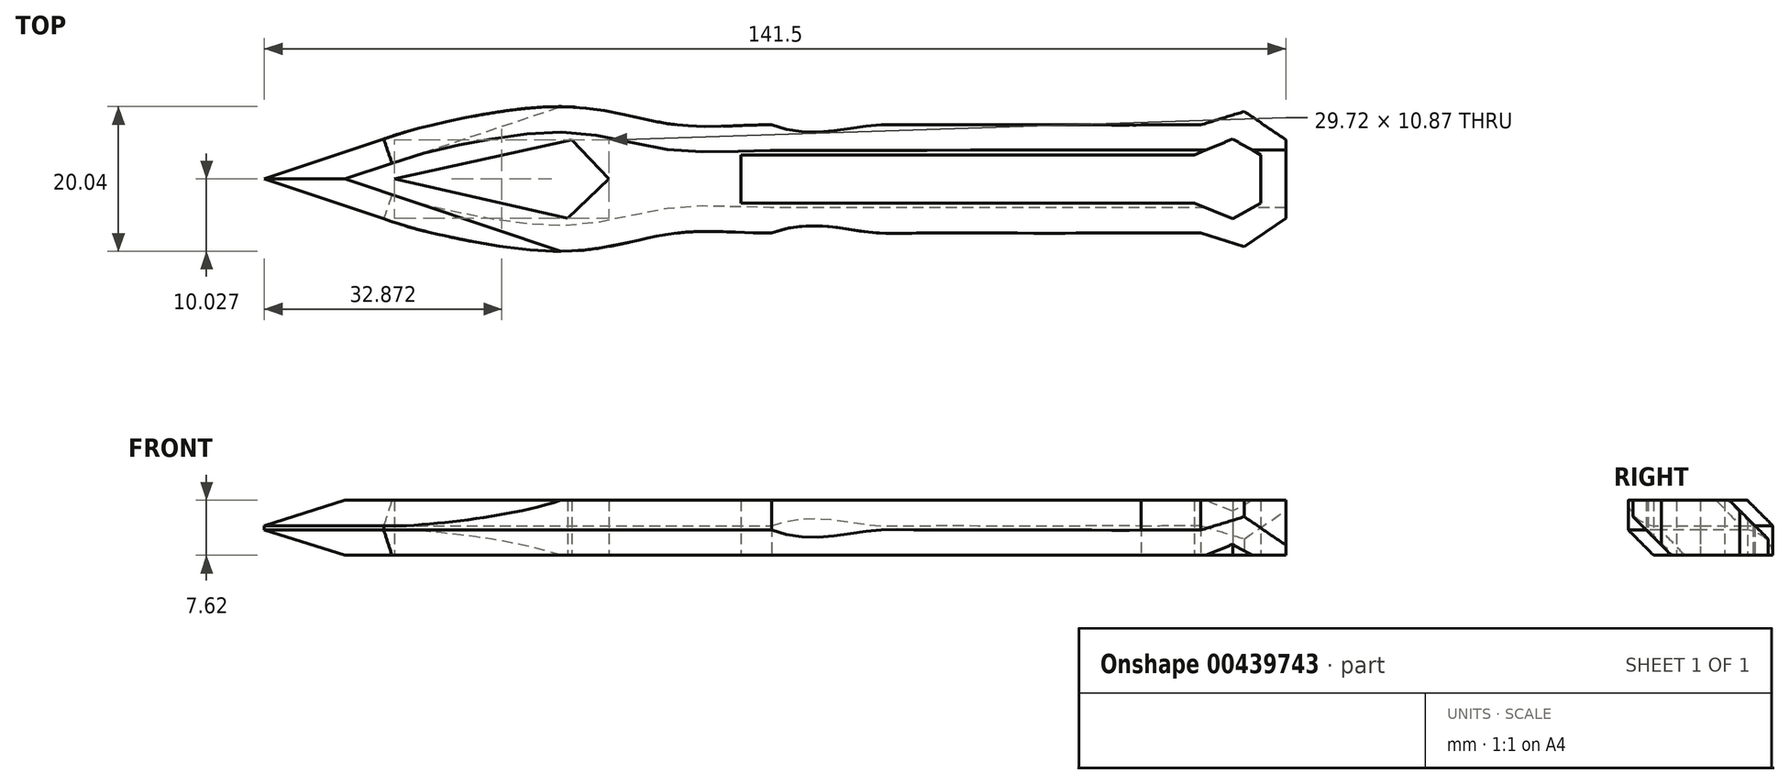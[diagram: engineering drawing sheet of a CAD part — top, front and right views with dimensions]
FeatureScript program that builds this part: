
annotation { "Feature Type Name" : "Feature", "Feature Type Description" : "" }
export const myFeature = defineFeature(function(context is Context, id is Id, definition is map)
    precondition{}
    {
        {
            var Q0;
            Q0=qCreatedBy(makeId("Top.planeOp"),FACE);
            var sketch = newSketch(context, id + "F0", { "sketchPlane" : qUnion([Q0])});
            skLineSegment(sketch, "E0", {"start": v(-70.25, 0) * mm, "end": v(-53.73, 5.53) * mm});
            skFitSpline(sketch, "E1", {"points": [v(-53.73, 5.53) * mm, v(-46.23, 7.66) * mm, v(-27.9, 9.99) * mm, v(-13.2, 7.5) * mm, v(0, 7.5) * mm], "startDerivative": vector(45.2, 15.8) * mm, "endDerivative": vector(54.18, 0.03) * mm});
            skFitSpline(sketch, "E2", {"points": [v(0, 7.5) * mm, v(12.65, 7.26) * mm, v(20.34, 7.5) * mm, v(42.69, 7.5) * mm, v(51.18, 7.5) * mm], "startDerivative": vector(56.8, -21.67) * mm, "endDerivative": vector(32.3, 1.6) * mm});
            skLineSegment(sketch, "E3.MirrorCS", {"start": v(-70.25, 0) * mm, "end": v(-53.73, -5.53) * mm});
            skFitSpline(sketch, "E4.MirrorCS", {"points": [v(-53.73, -5.53) * mm, v(-46.23, -7.66) * mm, v(-27.9, -9.99) * mm, v(-13.2, -7.5) * mm, v(0, -7.5) * mm], "startDerivative": vector(45.2, -15.8) * mm, "endDerivative": vector(54.18, -0.03) * mm});
            skFitSpline(sketch, "E5.MirrorCS", {"points": [v(0, -7.5) * mm, v(12.65, -7.26) * mm, v(20.34, -7.5) * mm, v(42.69, -7.5) * mm, v(51.18, -7.5) * mm], "startDerivative": vector(56.8, 21.67) * mm, "endDerivative": vector(32.3, -1.6) * mm});
            skLineSegment(sketch, "E6", {"start": v(51.18, 7.5) * mm, "end": v(59.48, 7.5) * mm});
            skLineSegment(sketch, "E7", {"start": v(59.48, 7.5) * mm, "end": v(65.48, 9.35) * mm});
            skLineSegment(sketch, "E8", {"start": v(65.48, 9.35) * mm, "end": v(71.25, 5.43) * mm});
            skLineSegment(sketch, "E9", {"start": v(71.25, 5.43) * mm, "end": v(71.25, 0) * mm});
            skLineSegment(sketch, "E10.MirrorCS", {"start": v(51.18, -7.5) * mm, "end": v(59.48, -7.5) * mm});
            skLineSegment(sketch, "E11.MirrorCS", {"start": v(59.48, -7.5) * mm, "end": v(65.48, -9.35) * mm});
            skLineSegment(sketch, "E12.MirrorCS", {"start": v(65.48, -9.35) * mm, "end": v(71.25, -5.43) * mm});
            skLineSegment(sketch, "E13.MirrorCS", {"start": v(71.25, -5.43) * mm, "end": v(71.25, 0) * mm});
            skLineSegment(sketch, "E14", {"start": v(-4.23, 3.34) * mm, "end": v(4.77, 3.34) * mm});
            skLineSegment(sketch, "E15", {"start": v(4.77, 3.34) * mm, "end": v(58.55, 3.34) * mm});
            skLineSegment(sketch, "E16", {"start": v(58.55, 3.34) * mm, "end": v(63.86, 5.53) * mm});
            skLineSegment(sketch, "E17", {"start": v(63.86, 5.53) * mm, "end": v(67.79, 3.34) * mm});
            skLineSegment(sketch, "E18", {"start": v(67.79, 3.34) * mm, "end": v(67.79, 0) * mm});
            skLineSegment(sketch, "E19.MirrorCS", {"start": v(-4.23, -3.34) * mm, "end": v(4.77, -3.34) * mm});
            skLineSegment(sketch, "E20.MirrorCS", {"start": v(4.77, -3.34) * mm, "end": v(58.55, -3.34) * mm});
            skLineSegment(sketch, "E21.MirrorCS", {"start": v(58.55, -3.34) * mm, "end": v(63.86, -5.53) * mm});
            skLineSegment(sketch, "E22.MirrorCS", {"start": v(63.86, -5.53) * mm, "end": v(67.79, -3.34) * mm});
            skLineSegment(sketch, "E23", {"start": v(67.79, 0) * mm, "end": v(67.79, -3.34) * mm});
            skLineSegment(sketch, "E24", {"start": v(-4.23, -3.34) * mm, "end": v(-4.23, 3.34) * mm});
            skLineSegment(sketch, "E25", {"start": v(-28.22, -5.43) * mm, "end": v(-22.52, 0) * mm});
            skLineSegment(sketch, "E26", {"start": v(-22.52, 0) * mm, "end": v(-27.7, 5.44) * mm});
            skLineSegment(sketch, "E27", {"start": v(-27.7, 5.44) * mm, "end": v(-52.24, 0) * mm});
            skLineSegment(sketch, "E28", {"start": v(-52.24, 0) * mm, "end": v(-28.22, -5.43) * mm});
            skSolve(sketch);
        }
        {
            var Q0;
            Q0 = qSketchRegion(id + "F0", true);
            extrude(context, id + "F1", {"entities" : qUnion([Q0]), "depth" : 7.62 * mm});
        }
        {
            var Q0;
            Q0=makeQuery(id+"F1.opExtrude","CAP_EDGE",EDGE,{"disambiguationData":[OSD([sQuery(id+"F0.wireOp",EDGE,"E0")])],"isStart":true});
            var Q1;
            Q1=makeQuery(id+"F1.opExtrude","CAP_EDGE",EDGE,{"disambiguationData":[OSD([sQuery(id+"F0.wireOp",EDGE,"E0")])],"isStart":false});
            var Q2;
            Q2=makeQuery(id+"F1.opExtrude","CAP_EDGE",EDGE,{"disambiguationData":[OSD([sQuery(id+"F0.wireOp",EDGE,"E3.MirrorCS")])],"isStart":false});
            var Q3;
            Q3=makeQuery(id+"F1.opExtrude","CAP_EDGE",EDGE,{"disambiguationData":[OSD([sQuery(id+"F0.wireOp",EDGE,"E3.MirrorCS")])],"isStart":true});
            chamfer(context, id + "F2", {"entities" : qUnion([Q0, Q1, Q2, Q3]), "width" : 3.53 * mm, "tangentPropagation" : true});
        }
    });
